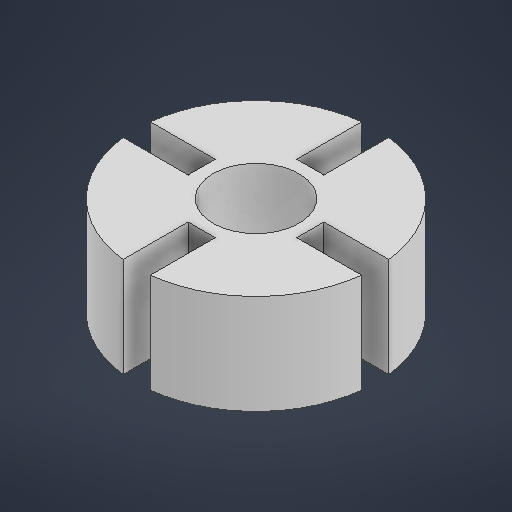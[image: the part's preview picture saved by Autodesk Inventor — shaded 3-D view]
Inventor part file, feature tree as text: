
AUTODESK INVENTOR PART (.ipt)
format: ipt  version: 2025.3 (Build 293356000, 356)  size: 201,728 bytes
history: native  units: mm
features: sketch x2, extrude x1
ambient origin geometry x8: Origin, YZ Plane, XZ Plane, XY Plane, X Axis, Y Axis, Z Axis, Center Point
bodies: Solid1 (feature_tree)
feature tree (3):
  extrude  "Extrusion1"  Depth=6.0mm
  sketch  "Sketch1"  dims[d0=53.0mm d1=6.0mm]
  sketch  "Sketch Circular Pattern1"  dims[d3=19.0mm d4=12.0mm d5=15.0mm d6=40.0mm d8=360.0deg d10=22.0mm d11=0.0mm]
